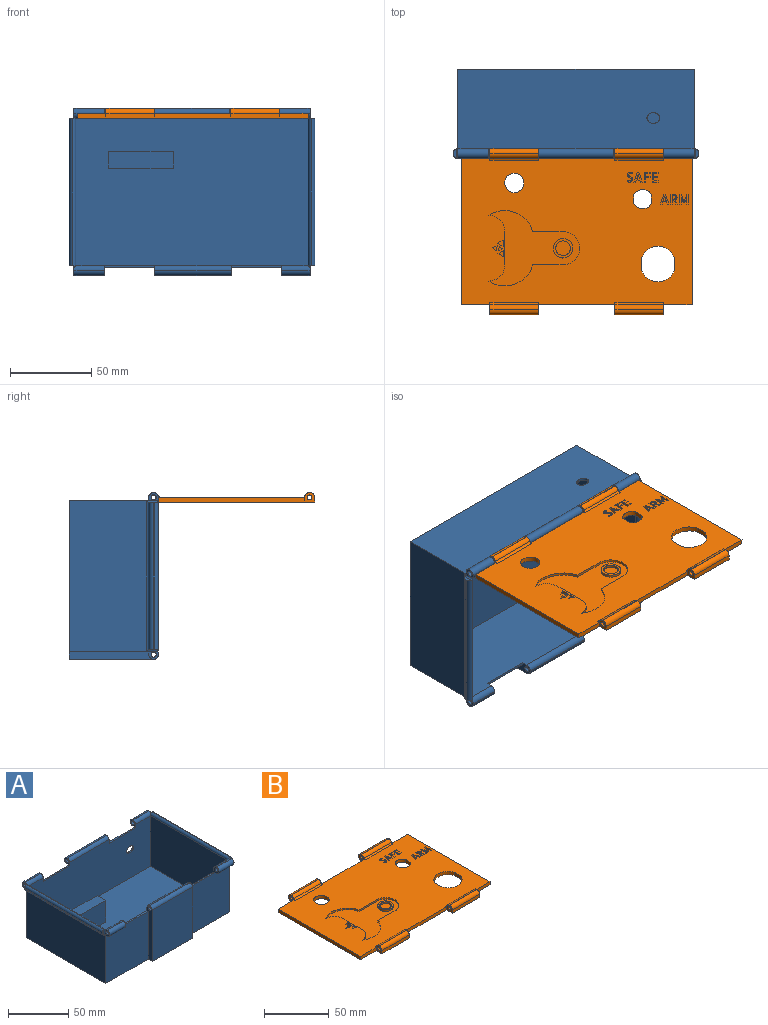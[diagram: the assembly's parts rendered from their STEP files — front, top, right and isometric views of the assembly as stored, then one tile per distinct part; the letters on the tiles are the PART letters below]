
ASSEMBLY  parts=2 mates=1
PART A: 77 faces, bbox 151.4x102.9x55 mm
  f0: plane 18.7x0.2mm, normal (0,0,1), area 3.7mm2, adj f2,f25,f46,f54
  f1: plane 18.7x0.2mm, normal (0,0,1), area 3.7mm2, adj f16,f17,f48,f51
  f2: plane 102.9x55mm, normal (1,0,0), area 4488.1mm2, adj f0,f3,f5,f7,f27,f37,f39,f46
  f3: plane 49x48.5mm, normal (0,-1,0), area 2361mm2, adj f2,f7,f20,f26,f32,f39
  f4: plane 49.7x49mm, normal (0,-1,0), area 2419.8mm2, adj f7,f17,f18,f21,f31,f38
  f5: plane 145.4x49mm, normal (0,1,0), area 7052.8mm2, adj f2,f7,f16,f17,f25,f28,f29,f33
  f6: plane 143x90.5mm, normal (0,0,1), area 12541.5mm2, adj f9,f10,f11,f12,f13,f14,f15,f24
  f7: plane 145.4x98.1mm, normal (0,0,-1), area 13792.4mm2, adj f2,f3,f4,f5,f17,f20,f21,f22
  f8: plane 40x10mm, normal (0,0,1), area 400mm2, adj f9,f10,f11,f12
  f9: plane 22x10mm, normal (1,0,0), area 220mm2, adj f6,f8,f10,f12
  f10: plane 40x22mm, normal (0,1,0), area 880mm2, adj f6,f8,f9,f11
  f11: plane 22x10mm, normal (-1,0,0), area 220mm2, adj f6,f8,f10,f12
  f12: plane 40x22mm, normal (0,-1,0), area 880mm2, adj f6,f8,f9,f11
  f13: plane 143x51mm, normal (0,-1,0), area 7035.2mm2, adj f6,f14,f16,f24,f25,f28,f29,f33
  f14: plane 90.52x51.25mm, normal (1,0,0), area 4638.1mm2, adj f6,f13,f15,f51,f52,f68
  f15: plane 143x51mm, normal (0,1,0), area 7076mm2, adj f6,f14,f18,f20,f21,f24,f26,f31
  f16: plane 6.5x6.2mm, normal (1,0,0), area 24.1mm2, adj f1,f5,f13,f33,f35,f48,f51,f60
  f17: plane 102.9x55mm, normal (-1,0,0), area 4488.1mm2, adj f1,f4,f5,f7,f19,f35,f38,f48
  f18: plane 6.5x6.2mm, normal (1,0,0), area 24.1mm2, adj f4,f15,f19,f31,f38,f50,f52,f63
  f19: plane 18.7x0.2mm, normal (0,0,1), area 3.7mm2, adj f17,f18,f50,f52
  f20: plane 55x6.2mm, normal (1,0,0), area 261.2mm2, adj f3,f7,f15,f22,f23,f32,f56,f57
  f21: plane 55x6.2mm, normal (-1,0,0), area 261.2mm2, adj f4,f7,f15,f22,f23,f31,f56,f57
  f22: plane 52x47.2mm, normal (0,-1,0), area 2454.4mm2, adj f7,f20,f21,f57
  f23: plane 47.2x0.2mm, normal (0,0,1), area 9.4mm2, adj f20,f21,f56,f57
  f24: plane 90.52x51.25mm, normal (-1,0,0), area 4638.1mm2, adj f6,f13,f15,f54,f55,f65
  f25: plane 6.5x6.2mm, normal (-1,0,0), area 24.1mm2, adj f0,f5,f13,f34,f37,f46,f54,f59
  f26: plane 6.5x6.2mm, normal (-1,0,0), area 24.1mm2, adj f3,f15,f27,f32,f39,f49,f55,f61
  f27: plane 17.5x0.2mm, normal (0,0,1), area 3.5mm2, adj f2,f26,f49,f55
  f28: plane 6.5x6.2mm, normal (1,0,0), area 24.1mm2, adj f5,f13,f30,f34,f36,f47,f53,f58
  f29: plane 6.5x6.2mm, normal (-1,0,0), area 24.1mm2, adj f5,f13,f30,f33,f36,f47,f53,f58
  f30: plane 46x0.2mm, normal (0,0,1), area 9.2mm2, adj f28,f29,f47,f53
  f31: plane 31x1.4mm, normal (0,0,1), area 43.4mm2, adj f4,f15,f18,f21
  f32: plane 31x1.4mm, normal (0,0,1), area 43.4mm2, adj f3,f15,f20,f26
  f33: plane 31x1.4mm, normal (0,0,1), area 43.4mm2, adj f5,f13,f16,f29
  f34: plane 31x1.4mm, normal (0,0,1), area 43.4mm2, adj f5,f13,f25,f28
  f35: plane 18.7x1.8mm, normal (0,0,-1), area 33.7mm2, adj f5,f16,f17,f48
  f36: plane 46x1.8mm, normal (0,0,-1), area 82.8mm2, adj f5,f28,f29,f47
  f37: plane 18.7x1.8mm, normal (0,0,-1), area 33.7mm2, adj f2,f5,f25,f46
  f38: plane 18.7x1.8mm, normal (0,0,-1), area 33.7mm2, adj f4,f17,f18,f50
  f39: plane 17.5x1.8mm, normal (0,0,-1), area 31.5mm2, adj f2,f3,f26,f49
  f40: plane 5.79x2mm, normal (0,-1,0), area 8.8mm2, adj f41,f64,f66,f72,f75
  f41: plane 90.5x0.5mm, normal (1,0,0), area 45.3mm2, adj f40,f42,f64,f66
  f42: plane 5.79x2mm, normal (0,1,0), area 8.8mm2, adj f41,f64,f66,f73,f75
  f43: plane 5.79x2mm, normal (0,-1,0), area 8.8mm2, adj f45,f67,f69,f70,f76
  f44: plane 5.79x2mm, normal (0,1,0), area 8.8mm2, adj f45,f67,f69,f71,f76
  f45: plane 90.5x0.5mm, normal (-1,0,0), area 45.3mm2, adj f43,f44,f67,f69
  f46: cylinder r=3mm len=18.7mm, axis (1,0,0), area 176.2mm2, adj f0,f2,f25,f37
  f47: cylinder r=3mm len=46mm, axis (1,0,0), area 433.5mm2, adj f28,f29,f30,f36
  f48: cylinder r=3mm len=18.7mm, axis (1,0,0), area 176.2mm2, adj f1,f16,f17,f35
  f49: cylinder r=3mm len=17.5mm, axis (-1,0,0), area 164.9mm2, adj f2,f26,f27,f39
  f50: cylinder r=3mm len=18.7mm, axis (-1,0,0), area 176.2mm2, adj f17,f18,f19,f38
  f51: cylinder r=3mm len=18.7mm, axis (-1,0,0), area 85.7mm2, adj f1,f13,f14,f16,f17,f68
  f52: cylinder r=3mm len=18.7mm, axis (1,0,0), area 85.7mm2, adj f14,f15,f17,f18,f19,f68
  f53: cylinder r=3mm len=46mm, axis (-1,0,0), area 216.8mm2, adj f13,f28,f29,f30
  f54: cylinder r=3mm len=18.7mm, axis (-1,0,0), area 85.7mm2, adj f0,f2,f13,f24,f25,f65
  f55: cylinder r=3mm len=17.5mm, axis (1,0,0), area 80mm2, adj f2,f15,f24,f26,f27,f65
  f56: cylinder r=3mm len=47.2mm, axis (1,0,0), area 222.4mm2, adj f15,f20,f21,f23
  f57: cylinder r=3mm len=47.2mm, axis (-1,0,0), area 222.4mm2, adj f20,f21,f22,f23
  f58: cylinder r=1.6mm len=46mm, axis (-1,0,0), area 462.4mm2, adj f28,f29
  f59: cylinder r=1.6mm len=18.7mm, axis (-1,0,0), area 188mm2, adj f2,f25
  f60: cylinder r=1.6mm len=18.7mm, axis (-1,0,0), area 188mm2, adj f16,f17
  f61: cylinder r=1.6mm len=17.5mm, axis (-1,0,0), area 175.9mm2, adj f2,f26
  f62: cylinder r=1.6mm len=47.2mm, axis (-1,0,0), area 474.5mm2, adj f20,f21
  f63: cylinder r=1.6mm len=18.7mm, axis (-1,0,0), area 188mm2, adj f17,f18
  f64: cylinder r=2.75mm len=90.5mm, axis (0,1,0), area 316.6mm2, adj f40,f41,f42,f75
  f65: cylinder r=2.75mm len=93.25mm, axis (0,1,0), area 334.8mm2, adj f2,f24,f54,f55,f66,f72,f73
  f66: cylinder r=2.75mm len=90.51mm, axis (0,-1,0), area 331.5mm2, adj f40,f41,f42,f65,f72,f73
  f67: cylinder r=2.75mm len=90.5mm, axis (0,-1,0), area 316.6mm2, adj f43,f44,f45,f76
  f68: cylinder r=2.75mm len=93.25mm, axis (0,-1,0), area 334.8mm2, adj f14,f17,f51,f52,f69,f70,f71
  f69: cylinder r=2.75mm len=90.51mm, axis (0,1,0), area 331.5mm2, adj f43,f44,f45,f68,f70,f71
  f70: cylinder r=1mm len=7.23mm, axis (0,0,1), area 9.7mm2, adj f17,f43,f68,f69,f76
  f71: cylinder r=1mm len=7.23mm, axis (0,0,-1), area 9.7mm2, adj f17,f44,f68,f69,f76
  f72: cylinder r=1mm len=7.23mm, axis (0,0,1), area 9.7mm2, adj f2,f40,f65,f66,f75
  f73: cylinder r=1mm len=7.23mm, axis (0,0,-1), area 9.7mm2, adj f2,f42,f65,f66,f75
  f74: extruded ~8x6.5mm, area 32mm2, adj f5,f13
  f75: cylinder r=1.5mm len=92.5mm, axis (0,1,0), area 174.1mm2, adj f2,f40,f42,f64,f72,f73
  f76: cylinder r=1.5mm len=92.5mm, axis (0,-1,0), area 174.1mm2, adj f17,f43,f44,f67,f70,f71
PART B: 247 faces, bbox 142x102.4x6 mm
  f0: plane 2.92x1.5mm, normal (0.39,-0.92,0), area 4.8mm2, adj f1,f2,f197,f225
  f1: plane 3.15x1.5mm, normal (-0.99,0.12,0), area 4.8mm2, adj f0,f2,f197,f225
  f2: plane 2.54x1.9mm, normal (0.6,0.8,0), area 4.8mm2, adj f0,f1,f197,f225
  f3: plane 2.59x1.5mm, normal (0.99,-0.14,0), area 3.9mm2, adj f4,f5,f197,f224
  f4: plane 2.06x1.61mm, normal (-0.62,-0.79,0), area 3.9mm2, adj f3,f5,f197,f224
  f5: plane 2.43x1.5mm, normal (-0.37,0.93,0), area 3.9mm2, adj f3,f4,f197,f224
  f6: plane 3.45x1.93mm, normal (0.49,-0.87,0), area 5.9mm2, adj f7,f8,f197,f223
  f7: plane 3.95x1.5mm, normal (-1,0.01,0), area 5.9mm2, adj f6,f8,f197,f223
  f8: plane 3.4x2.02mm, normal (0.51,0.86,0), area 5.9mm2, adj f6,f7,f197,f223
  f9: plane 3.45x1.91mm, normal (0.48,-0.88,0), area 5.9mm2, adj f10,f11,f197,f222
  f10: plane 3.94x1.5mm, normal (-1,0.02,0), area 5.9mm2, adj f9,f11,f197,f222
  f11: plane 3.38x2.04mm, normal (0.52,0.86,0), area 5.9mm2, adj f9,f10,f197,f222
  f12: plane 1.5x0.74mm, normal (1,0,0), area 1.1mm2, adj f13,f15,f197,f221
  f13: plane 2.42x1.5mm, normal (0,-1,0), area 3.6mm2, adj f12,f14,f197,f221
  f14: plane 1.5x0.74mm, normal (-1,0,0), area 1.1mm2, adj f13,f15,f197,f221
  f15: plane 2.42x1.5mm, normal (0,1,0), area 3.6mm2, adj f12,f14,f197,f221
  f16: plane 2.42x1.5mm, normal (0,1,0), area 3.6mm2, adj f17,f19,f197,f220
  f17: plane 1.5x0.74mm, normal (1,0,0), area 1.1mm2, adj f16,f18,f197,f220
  f18: plane 2.42x1.5mm, normal (0,-1,0), area 3.6mm2, adj f17,f19,f197,f220
  f19: plane 1.5x0.74mm, normal (-1,0,0), area 1.1mm2, adj f16,f18,f197,f220
  f20: plane 2.17x1.5mm, normal (0,-1,0), area 3.3mm2, adj f21,f23,f197,f219
  f21: plane 1.5x0.67mm, normal (-1,0,0), area 1mm2, adj f20,f22,f197,f219
  f22: plane 2.17x1.5mm, normal (0,1,0), area 3.3mm2, adj f21,f23,f197,f219
  f23: plane 1.5x0.67mm, normal (1,0,0), area 1mm2, adj f20,f22,f197,f219
  f24: plane 1.5x0.99mm, normal (0,1,0), area 1.5mm2, adj f25,f27,f197,f218
  f25: plane 6x1.5mm, normal (1,0,0), area 9mm2, adj f24,f26,f197,f218
  f26: plane 1.5x0.99mm, normal (0,-1,0), area 1.5mm2, adj f25,f27,f197,f218
  f27: plane 6x1.5mm, normal (-1,0,0), area 9mm2, adj f24,f26,f197,f218
  f28: plane 1.5x0.74mm, normal (1,0,0), area 1.1mm2, adj f29,f31,f197,f217
  f29: plane 2.42x1.5mm, normal (0,-1,0), area 3.6mm2, adj f28,f30,f197,f217
  f30: plane 1.5x0.74mm, normal (-1,0,0), area 1.1mm2, adj f29,f31,f197,f217
  f31: plane 2.42x1.5mm, normal (0,1,0), area 3.6mm2, adj f28,f30,f197,f217
  f32: plane 2.17x1.5mm, normal (0,-1,0), area 3.3mm2, adj f33,f35,f197,f216
  f33: plane 1.5x0.67mm, normal (-1,0,0), area 1mm2, adj f32,f34,f197,f216
  f34: plane 2.17x1.5mm, normal (0,1,0), area 3.3mm2, adj f33,f35,f197,f216
  f35: plane 1.5x0.67mm, normal (1,0,0), area 1mm2, adj f32,f34,f197,f216
  f36: plane 1.5x0.99mm, normal (0,1,0), area 1.5mm2, adj f37,f39,f197,f215
  f37: plane 6x1.5mm, normal (1,0,0), area 9mm2, adj f36,f38,f197,f215
  f38: plane 1.5x0.99mm, normal (0,-1,0), area 1.5mm2, adj f37,f39,f197,f215
  f39: plane 6x1.5mm, normal (-1,0,0), area 9mm2, adj f36,f38,f197,f215
  f40: plane 1.5x0.66mm, normal (0.95,-0.33,0), area 1mm2, adj f41,f43,f197,f214
  f41: plane 1.5x1.09mm, normal (0,-1,0), area 1.6mm2, adj f40,f42,f197,f214
  f42: plane 1.5x0.66mm, normal (-0.94,-0.34,0), area 1.1mm2, adj f41,f43,f197,f214
  f43: plane 1.55x1.5mm, normal (0,1,0), area 2.3mm2, adj f40,f42,f197,f214
  f44: plane 1.5x0.97mm, normal (0,-1,0), area 1.5mm2, adj f45,f48,f197,f213
  f45: plane 5.99x2.08mm, normal (-0.94,-0.33,0), area 9.5mm2, adj f44,f46,f197,f213
  f46: plane 1.5x1.01mm, normal (0,1,0), area 1.5mm2, adj f45,f148,f197,f213
  f47: plane 1.5x1.02mm, normal (0,1,0), area 1.5mm2, adj f48,f149,f197,f213
  f48: plane 5.99x2.1mm, normal (0.94,-0.33,0), area 9.5mm2, adj f44,f47,f197,f213
  f49: plane 1.5x0.95mm, normal (1,0,0), area 1.4mm2, adj f50,f150,f197,f212
  f50: extruded ~1.5x0.55mm, area 0.9mm2, adj f49,f51,f197,f212
  f51: extruded ~1.5x0.51mm, area 0.9mm2, adj f50,f52,f197,f212
  f52: extruded ~1.5x0.48mm, area 0.9mm2, adj f51,f53,f197,f212
  f53: extruded ~1.5x0.71mm, area 1.1mm2, adj f52,f54,f197,f212
  f54: extruded ~1.5x0.57mm, area 0.9mm2, adj f53,f55,f197,f212
  f55: extruded ~1.5x0.5mm, area 0.9mm2, adj f54,f56,f197,f212
  f56: extruded ~1.5x0.49mm, area 0.9mm2, adj f55,f57,f197,f212
  f57: extruded ~1.5x0.67mm, area 1.1mm2, adj f56,f58,f197,f212
  f58: plane 1.5x0.78mm, normal (1,0,0), area 1.2mm2, adj f57,f151,f197,f212
  f59: extruded ~1.5x0.33mm, area 0.6mm2, adj f60,f70,f197,f211
  f60: plane 1.5x0.7mm, normal (0.97,-0.24,0), area 1.1mm2, adj f59,f61,f197,f211
  f61: extruded ~1.5x0.29mm, area 0.5mm2, adj f60,f62,f197,f211
  f62: extruded ~1.5x0.36mm, area 0.6mm2, adj f61,f63,f197,f211
  f63: extruded ~1.5x0.37mm, area 0.6mm2, adj f62,f64,f197,f211
  f64: extruded ~1.5x0.35mm, area 0.5mm2, adj f63,f65,f197,f211
  f65: plane 1.5x0.02mm, normal (0,-1,0), area 0mm2, adj f64,f66,f197,f211
  f66: plane 1.5x0.77mm, normal (-1,0,0), area 1.2mm2, adj f65,f67,f197,f211
  f67: plane 1.5x0.02mm, normal (0,1,0), area 0mm2, adj f66,f68,f197,f211
  f68: extruded ~1.5x0.4mm, area 0.6mm2, adj f67,f69,f197,f211
  f69: extruded ~1.5x0.42mm, area 0.6mm2, adj f68,f70,f197,f211
  f70: extruded ~1.5x0.4mm, area 0.6mm2, adj f59,f69,f197,f211
  f71: extruded ~1.5x0.47mm, area 0.9mm2, adj f72,f80,f197,f210
  f72: extruded ~1.5x0.64mm, area 1mm2, adj f71,f73,f197,f210
  f73: extruded ~1.5x0.64mm, area 1mm2, adj f72,f74,f197,f210
  f74: extruded ~1.5x0.5mm, area 0.9mm2, adj f73,f75,f197,f210
  f75: extruded ~1.5x0.49mm, area 0.9mm2, adj f74,f76,f197,f210
  f76: extruded ~1.5x0.59mm, area 0.9mm2, adj f75,f77,f197,f210
  f77: plane 1.5x0.86mm, normal (-1,0,0), area 1.3mm2, adj f76,f152,f197,f210
  f78: plane 1.5x0.93mm, normal (-1,0,0), area 1.4mm2, adj f79,f155,f197,f210
  f79: extruded ~1.5x0.54mm, area 0.9mm2, adj f78,f80,f197,f210
  f80: extruded ~1.5x0.49mm, area 0.9mm2, adj f71,f79,f197,f210
  f81: extruded ~1.5x0.18mm, area 0.3mm2, adj f82,f88,f197,f209
  f82: extruded ~1.5x0.08mm, area 0.1mm2, adj f81,f83,f197,f209
  f83: extruded ~1.5x0.1mm, area 0.2mm2, adj f82,f156,f197,f209
  f84: plane 1.5x0.82mm, normal (1,0,0), area 1.2mm2, adj f85,f158,f197,f209
  f85: extruded ~1.5x0.73mm, area 1.1mm2, adj f84,f86,f197,f209
  f86: extruded ~1.5x0.6mm, area 1mm2, adj f85,f87,f197,f209
  f87: extruded ~1.5x0.23mm, area 0.4mm2, adj f86,f88,f197,f209
  f88: extruded ~1.5x0.24mm, area 0.4mm2, adj f81,f87,f197,f209
  f89: plane 1.5x1.49mm, normal (1,0,0), area 2.2mm2, adj f90,f94,f197,f208
  f90: plane 3.72x1.61mm, normal (0.92,-0.4,0), area 6.1mm2, adj f89,f91,f197,f208
  f91: plane 1.5x0.99mm, normal (0,-1,0), area 1.5mm2, adj f90,f92,f197,f208
  f92: plane 6x1.5mm, normal (-1,0,0), area 9mm2, adj f91,f93,f197,f208
  f93: plane 1.5x0.99mm, normal (0,1,0), area 1.5mm2, adj f92,f159,f197,f208
  f94: plane 1.5x0.27mm, normal (0,1,0), area 0.4mm2, adj f89,f160,f197,f208
  f95: plane 1.5x0.99mm, normal (0,1,0), area 1.5mm2, adj f96,f192,f197,f207
  f96: plane 6x1.5mm, normal (1,0,0), area 9mm2, adj f95,f97,f197,f207
  f97: plane 1.5x0.99mm, normal (0,-1,0), area 1.5mm2, adj f96,f98,f197,f207
  f98: plane 3.7x1.61mm, normal (-0.92,-0.4,0), area 6.1mm2, adj f97,f99,f197,f207
  f99: plane 1.51x1.5mm, normal (-1,0,0), area 2.3mm2, adj f98,f100,f197,f207
  f100: plane 1.5x0.26mm, normal (0,1,0), area 0.4mm2, adj f99,f161,f197,f207
  f101: plane 1.5x1.03mm, normal (0,1,0), area 1.6mm2, adj f163,f164,f197,f206
  f102: extruded ~1.5x0.09mm, area 0.1mm2, adj f103,f165,f197,f206
  f103: plane 1.5x0.17mm, normal (0,1,0), area 0.3mm2, adj f102,f104,f197,f206
  f104: plane 1.5x0.29mm, normal (0,1,0), area 0.4mm2, adj f103,f105,f197,f206
  f105: plane 1.5x0.72mm, normal (1,0,0), area 1.1mm2, adj f104,f106,f197,f206
  f106: plane 1.5x0.55mm, normal (0,-1,0), area 0.8mm2, adj f105,f166,f197,f206
  f107: plane 1.5x0.4mm, normal (0,1,0), area 0.6mm2, adj f108,f173,f197,f206
  f108: plane 1.5x0.74mm, normal (1,0,0), area 1.1mm2, adj f107,f109,f197,f206
  f109: plane 1.5x0.42mm, normal (0,-1,0), area 0.6mm2, adj f108,f110,f197,f206
  f110: extruded ~1.5x0.76mm, area 1.2mm2, adj f109,f111,f197,f206
  f111: extruded ~1.5x0.67mm, area 1.2mm2, adj f110,f112,f197,f206
  f112: extruded ~1.5x0.59mm, area 1.1mm2, adj f111,f113,f197,f206
  f113: extruded ~1.5x0.78mm, area 1.2mm2, adj f112,f114,f197,f206
  f114: extruded ~1.5x1.11mm, area 1.7mm2, adj f113,f162,f197,f206
  f115: plane 1.5x0.98mm, normal (0,1,0), area 1.5mm2, adj f116,f118,f197,f205
  f116: plane 6x1.5mm, normal (1,0,0), area 9mm2, adj f115,f117,f197,f205
  f117: plane 1.5x0.98mm, normal (0,-1,0), area 1.5mm2, adj f116,f118,f197,f205
  f118: plane 6x1.5mm, normal (-1,0,0), area 9mm2, adj f115,f117,f197,f205
  f119: plane 1.5x0.66mm, normal (0.95,-0.33,0), area 1mm2, adj f120,f122,f197,f204
  f120: plane 1.5x1.09mm, normal (0,-1,0), area 1.6mm2, adj f119,f121,f197,f204
  f121: plane 1.5x0.66mm, normal (-0.94,-0.34,0), area 1.1mm2, adj f120,f122,f197,f204
  f122: plane 1.55x1.5mm, normal (0,1,0), area 2.3mm2, adj f119,f121,f197,f204
  f123: plane 1.5x0.97mm, normal (0,-1,0), area 1.5mm2, adj f124,f127,f197,f203
  f124: plane 5.99x2.08mm, normal (-0.94,-0.33,0), area 9.5mm2, adj f123,f125,f197,f203
  f125: plane 1.5x1.01mm, normal (0,1,0), area 1.5mm2, adj f124,f174,f197,f203
  f126: plane 1.5x1.02mm, normal (0,1,0), area 1.5mm2, adj f127,f175,f197,f203
  f127: plane 5.99x2.1mm, normal (0.94,-0.33,0), area 9.5mm2, adj f123,f126,f197,f203
  f128: cylinder r=10.26mm len=20.52mm, axis (0,0,1), area 48.3mm2, adj f184,f194,f197,f199
  f129: plane 7.44x6mm, normal (-1,0,0), area 27mm2, adj f130,f132,f133,f134,f197,f235,f236,f239
  f130: plane 30x3mm, normal (0,-1,0), area 90mm2, adj f129,f131,f133,f235
  f131: plane 7.44x6mm, normal (1,0,0), area 27mm2, adj f130,f132,f133,f177,f197,f235,f236,f239
  f132: plane 30x0.2mm, normal (0,0,1), area 6mm2, adj f129,f131,f235,f236
  f133: plane 142x99.4mm, normal (0,0,-1), area 12744.3mm2, adj f129,f130,f131,f134,f135,f136,f138,f139
  f134: plane 47x3mm, normal (0,-1,0), area 141mm2, adj f129,f133,f143,f197
  f135: plane 7.44x6mm, normal (1,0,0), area 25.1mm2, adj f133,f137,f142,f197,f232,f238,f240,f244
  f136: plane 7.44x6mm, normal (-1,0,0), area 25.1mm2, adj f133,f137,f138,f197,f232,f238,f240,f244
  f137: plane 30x0.2mm, normal (0,0,1), area 6mm2, adj f135,f136,f232,f238
  f138: plane 17.5x3mm, normal (0,1,0), area 52.5mm2, adj f133,f136,f176,f197
  f139: plane 7.44x6mm, normal (-1,0,0), area 25.1mm2, adj f133,f141,f142,f197,f231,f237,f241,f243
  f140: plane 7.44x6mm, normal (1,0,0), area 25.1mm2, adj f133,f141,f193,f197,f231,f237,f241,f243
  f141: plane 30x0.2mm, normal (0,0,1), area 6mm2, adj f139,f140,f231,f237
  f142: plane 47x3mm, normal (0,1,0), area 141mm2, adj f133,f135,f139,f197
  f143: plane 7.44x6mm, normal (1,0,0), area 27mm2, adj f133,f134,f145,f146,f197,f233,f234,f242
  f144: plane 7.44x6mm, normal (-1,0,0), area 27mm2, adj f133,f145,f146,f147,f197,f233,f234,f242
  f145: plane 30x3mm, normal (0,-1,0), area 90mm2, adj f133,f143,f144,f234
  f146: plane 30x0.2mm, normal (0,0,1), area 6mm2, adj f143,f144,f233,f234
  f147: plane 17.5x3mm, normal (0,-1,0), area 52.5mm2, adj f133,f144,f176,f197
  f148: plane 4.49x1.55mm, normal (0.95,0.33,0), area 7.1mm2, adj f46,f149,f197,f213
  f149: plane 4.49x1.57mm, normal (-0.94,0.33,0), area 7.1mm2, adj f47,f148,f197,f213
  f150: extruded ~1.5x0.48mm, area 0.9mm2, adj f49,f191,f197,f212
  f151: extruded ~1.5x0.89mm, area 1.8mm2, adj f58,f191,f197,f212
  f152: extruded ~1.5x0.43mm, area 0.8mm2, adj f77,f153,f197,f210
  f153: extruded ~1.5x0.45mm, area 0.7mm2, adj f152,f154,f197,f210
  f154: extruded ~1.5x0.51mm, area 0.8mm2, adj f153,f155,f197,f210
  f155: extruded ~1.5x0.43mm, area 0.8mm2, adj f78,f154,f197,f210
  f156: extruded ~1.5x0.16mm, area 0.3mm2, adj f83,f157,f197,f209
  f157: extruded ~1.5x0.27mm, area 0.4mm2, adj f156,f158,f197,f209
  f158: extruded ~1.5x0.42mm, area 0.6mm2, adj f84,f157,f197,f209
  f159: plane 4.13x1.5mm, normal (1,0,0), area 6.2mm2, adj f93,f160,f197,f208
  f160: plane 3.34x1.5mm, normal (-0.93,0.37,0), area 5.4mm2, adj f94,f159,f197,f208
  f161: plane 3.34x1.5mm, normal (0.93,0.38,0), area 5.4mm2, adj f100,f192,f197,f207
  f162: extruded ~1.5x0.81mm, area 1.6mm2, adj f114,f163,f197,f206
  f163: plane 2.36x1.5mm, normal (-0.87,-0.5,0), area 4.1mm2, adj f101,f162,f197,f206
  f164: plane 2.17x1.5mm, normal (0.89,0.46,0), area 3.7mm2, adj f101,f165,f197,f206
  f165: extruded ~1.5x0.05mm, area 0.1mm2, adj f102,f164,f197,f206
  f166: extruded ~1.5x0.36mm, area 0.5mm2, adj f106,f167,f197,f206
  f167: extruded ~1.5x0.33mm, area 0.6mm2, adj f166,f168,f197,f206
  f168: extruded ~1.5x0.39mm, area 0.7mm2, adj f167,f169,f197,f206
  f169: extruded ~1.5x0.61mm, area 0.9mm2, adj f168,f170,f197,f206
  f170: extruded ~1.5x0.34mm, area 0.5mm2, adj f169,f171,f197,f206
  f171: extruded ~1.5x0.37mm, area 0.6mm2, adj f170,f172,f197,f206
  f172: extruded ~1.5x0.35mm, area 0.7mm2, adj f171,f173,f197,f206
  f173: extruded ~1.5x0.6mm, area 0.9mm2, adj f107,f172,f197,f206
  f174: plane 4.49x1.55mm, normal (0.95,0.33,0), area 7.1mm2, adj f125,f175,f197,f203
  f175: plane 4.49x1.57mm, normal (-0.94,0.33,0), area 7.1mm2, adj f126,f174,f197,f203
  f176: plane 90x3mm, normal (-1,0,0), area 270mm2, adj f133,f138,f147,f197
  f177: plane 17.5x3mm, normal (0,-1,0), area 52.5mm2, adj f131,f133,f178,f197
  f178: plane 90x3mm, normal (1,0,0), area 270mm2, adj f133,f177,f193,f197
  f179: cylinder r=17.8mm len=27.05mm, axis (0,0,1), area 50.4mm2, adj f180,f194,f197,f199
  f180: cylinder r=9.93mm len=9.93mm, axis (0,0,1), area 23.4mm2, adj f179,f181,f197,f199
  f181: plane 20.52x1.5mm, normal (1,0,0), area 30.8mm2, adj f180,f182,f197,f199
  f182: cylinder r=9.93mm len=9.93mm, axis (0,0,1), area 23.4mm2, adj f181,f183,f197,f199
  f183: cylinder r=17.8mm len=27.05mm, axis (0,0,1), area 50.4mm2, adj f182,f184,f197,f199
  f184: plane 18.72x1.5mm, normal (0,-1,0), area 28.1mm2, adj f128,f183,f197,f199
  f185: cylinder r=10.9mm len=20.65mm, axis (0,0,1), area 81.4mm2, adj f133,f186,f195,f197
  f186: plane 6.99x3mm, normal (-1,0,0), area 21mm2, adj f133,f185,f187,f197
  f187: cylinder r=10.9mm len=20.65mm, axis (0,0,1), area 81.4mm2, adj f133,f186,f195,f197
  f188: plane 5.41x3mm, normal (-1,0,0), area 16.2mm2, adj f133,f189,f196,f197
  f189: cylinder r=5.95mm len=10.6mm, axis (0,0,1), area 39.2mm2, adj f133,f188,f190,f197
  f190: plane 5.41x3mm, normal (1,0,0), area 16.2mm2, adj f133,f189,f196,f197
  f191: extruded ~1.5x0.47mm, area 0.8mm2, adj f150,f151,f197,f212
  f192: plane 4.13x1.5mm, normal (-1,0,0), area 6.2mm2, adj f95,f161,f197,f207
  f193: plane 17.5x3mm, normal (0,1,0), area 52.5mm2, adj f133,f140,f178,f197
  f194: plane 18.72x1.5mm, normal (0,1,0), area 28.1mm2, adj f128,f179,f197,f199
  f195: plane 6.99x3mm, normal (1,0,0), area 21mm2, adj f133,f185,f187,f197
  f196: cylinder r=5.95mm len=10.6mm, axis (0,0,1), area 39.2mm2, adj f133,f188,f190,f197
  f197: plane 142x90mm, normal (0,0,1), area 10629.4mm2, adj f0,f1,f2,f3,f4,f5,f6,f7
  f198: plane 9x9mm, normal (0,0,1), area 63.6mm2, adj f202
  f199: plane 56.03x46.42mm, normal (0,0,1), area 1197.9mm2, adj f128,f179,f180,f181,f182,f183,f184,f194
  f200: plane 12x12mm, normal (0,0,1), area 49.5mm2, adj f201,f202
  f201: cylinder r=6mm len=12mm, axis (0,0,1), area 56.5mm2, adj f199,f200
  f202: cylinder r=4.5mm len=9mm, axis (0,0,1), area 42.4mm2, adj f198,f200
  f203: plane 5.99x5.15mm, normal (0,0,1), area 11.3mm2, adj f123,f124,f125,f126,f127,f174,f175
  f204: plane 1.55x0.66mm, normal (0,0,1), area 0.9mm2, adj f119,f120,f121,f122
  f205: plane 6x0.98mm, normal (0,0,1), area 5.9mm2, adj f115,f116,f117,f118
  f206: plane 6x2.76mm, normal (0,0,1), area 6.9mm2, adj f101,f102,f103,f104,f105,f106,f107,f108
  f207: plane 6x2.6mm, normal (0,0,1), area 9.1mm2, adj f95,f96,f97,f98,f99,f100,f161,f192
  f208: plane 6x2.6mm, normal (0,0,1), area 9.1mm2, adj f89,f90,f91,f92,f93,f94,f159,f160
  f209: plane 1.33x1.03mm, normal (0,0,1), area 1mm2, adj f81,f82,f83,f84,f85,f86,f87,f88
  f210: plane 3.4x1.53mm, normal (0,0,1), area 3.2mm2, adj f71,f72,f73,f74,f75,f76,f77,f78
  f211: plane 1.57x1.13mm, normal (0,0,1), area 1.2mm2, adj f59,f60,f61,f62,f63,f64,f65,f66
  f212: plane 3.44x1.58mm, normal (0,0,1), area 3.2mm2, adj f49,f50,f51,f52,f53,f54,f55,f56
  f213: plane 5.99x5.15mm, normal (0,0,1), area 11.3mm2, adj f44,f45,f46,f47,f48,f148,f149
  f214: plane 1.55x0.66mm, normal (0,0,1), area 0.9mm2, adj f40,f41,f42,f43
  f215: plane 6x0.99mm, normal (0,0,1), area 6mm2, adj f36,f37,f38,f39
  f216: plane 2.17x0.67mm, normal (0,0,1), area 1.5mm2, adj f32,f33,f34,f35
  f217: plane 2.42x0.74mm, normal (0,0,1), area 1.8mm2, adj f28,f29,f30,f31
  f218: plane 6x0.99mm, normal (0,0,1), area 6mm2, adj f24,f25,f26,f27
  f219: plane 2.17x0.67mm, normal (0,0,1), area 1.5mm2, adj f20,f21,f22,f23
  f220: plane 2.42x0.74mm, normal (0,0,1), area 1.8mm2, adj f16,f17,f18,f19
  f221: plane 2.42x0.74mm, normal (0,0,1), area 1.8mm2, adj f12,f13,f14,f15
  f222: plane 3.94x3.45mm, normal (0,0,1), area 6.7mm2, adj f9,f10,f11
  f223: plane 3.95x3.45mm, normal (0,0,1), area 6.8mm2, adj f6,f7,f8
  f224: plane 2.59x2.43mm, normal (0,0,1), area 3mm2, adj f3,f4,f5
  f225: plane 3.15x2.92mm, normal (0,0,1), area 4.4mm2, adj f0,f1,f2
  f226: cylinder r=5.95mm len=11.9mm, axis (0,0,-1), area 112.2mm2, adj f133,f197
  f227: cylinder r=1.5mm len=3mm, axis (0,0,1), area 14.1mm2, adj f133,f228
  f228: plane 3x3mm, normal (0,0,-1), area 7.1mm2, adj f227
  f229: cylinder r=1.5mm len=3mm, axis (0,0,1), area 14.1mm2, adj f133,f230
  f230: plane 3x3mm, normal (0,0,-1), area 7.1mm2, adj f229
  f231: cylinder r=3mm len=30mm, axis (-1,0,0), area 282.7mm2, adj f133,f139,f140,f141
  f232: cylinder r=3mm len=30mm, axis (-1,0,0), area 282.7mm2, adj f133,f135,f136,f137
  f233: cylinder r=3mm len=30mm, axis (1,0,0), area 110.8mm2, adj f143,f144,f146,f242
  f234: cylinder r=3mm len=30mm, axis (-1,0,0), area 141.4mm2, adj f143,f144,f145,f146
  f235: cylinder r=3mm len=30mm, axis (-1,0,0), area 141.4mm2, adj f129,f130,f131,f132
  f236: cylinder r=3mm len=30mm, axis (1,0,0), area 110.8mm2, adj f129,f131,f132,f239
  f237: cylinder r=3mm len=30mm, axis (-1,0,0), area 110.8mm2, adj f139,f140,f141,f241
  f238: cylinder r=3mm len=30mm, axis (-1,0,0), area 110.8mm2, adj f135,f136,f137,f240
  f239: cylinder r=1.5mm len=30mm, axis (1,0,0), area 55.4mm2, adj f129,f131,f197,f236
  f240: cylinder r=1.5mm len=30mm, axis (-1,0,0), area 55.4mm2, adj f135,f136,f197,f238
  f241: cylinder r=1.5mm len=30mm, axis (-1,0,0), area 55.4mm2, adj f139,f140,f197,f237
  f242: cylinder r=1.5mm len=30mm, axis (1,0,0), area 55.4mm2, adj f143,f144,f197,f233
  f243: cylinder r=1.45mm len=30mm, axis (-1,0,0), area 273.3mm2, adj f139,f140
  f244: cylinder r=1.45mm len=30mm, axis (-1,0,0), area 273.3mm2, adj f135,f136
  f245: cylinder r=1.45mm len=30mm, axis (-1,0,0), area 273.3mm2, adj f143,f144
  f246: cylinder r=1.45mm len=30mm, axis (-1,0,0), area 273.3mm2, adj f129,f131
PLACE A rot(axis=(1,0,0),90deg) t=(-58.8,102.72,36.36)mm
PLACE B rot(axis=(0.05,0.94,-0.35),0deg) t=(-58.3,2.72,83.31)mm
MATE revolute A.f46 <-> B.f237  axis (-1,0,0) through (-4.8,50.72,84.81)mm
